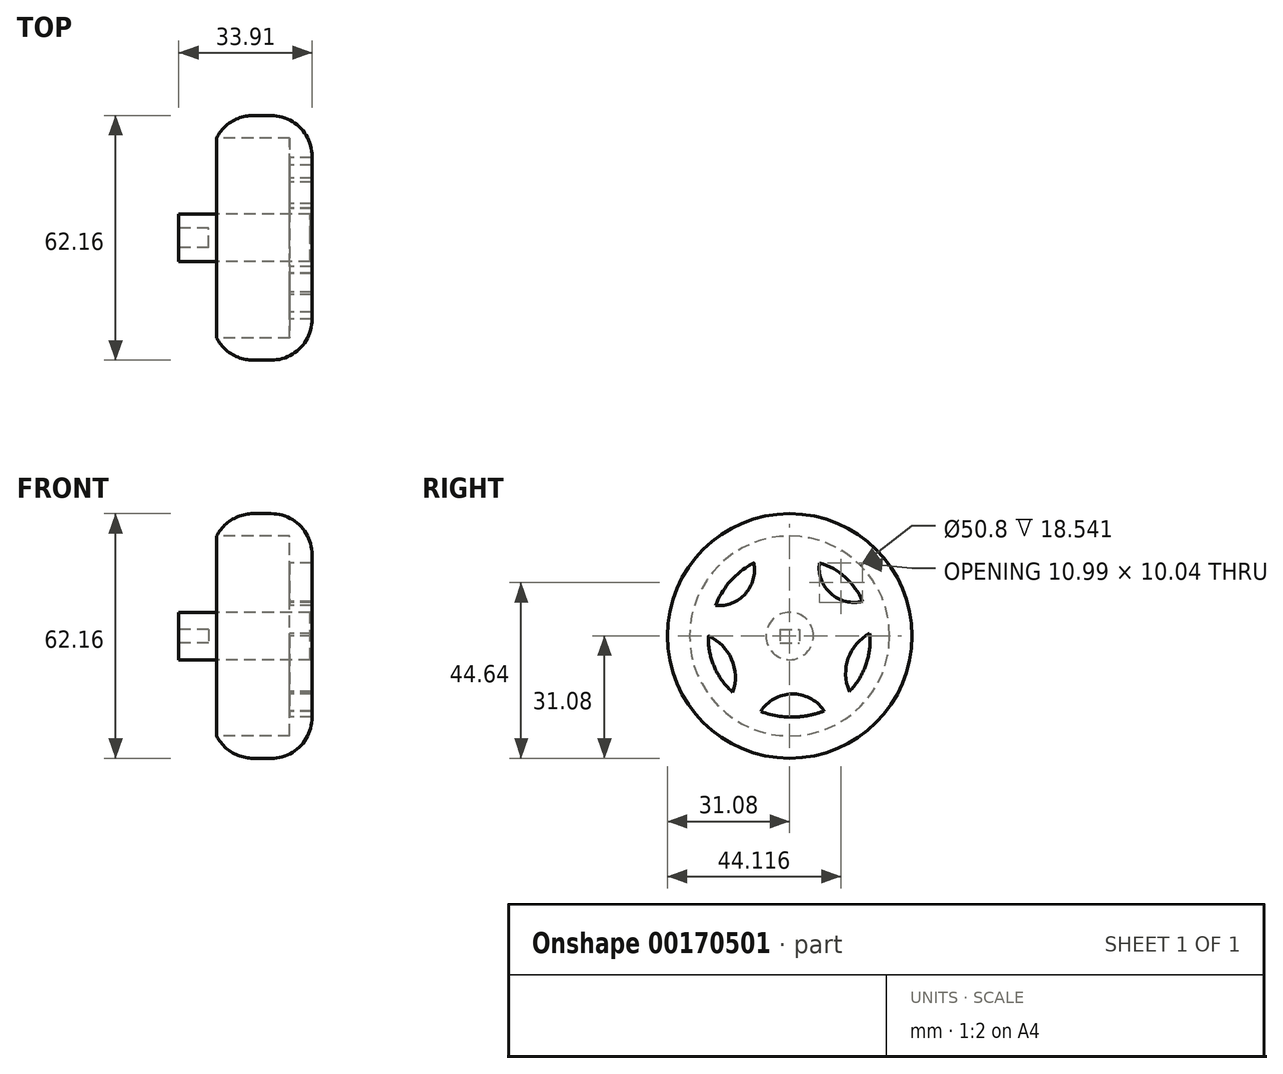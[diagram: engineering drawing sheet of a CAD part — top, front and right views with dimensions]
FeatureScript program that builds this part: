
annotation { "Feature Type Name" : "Feature", "Feature Type Description" : "" }
export const myFeature = defineFeature(function(context is Context, id is Id, definition is map)
    precondition{}
    {
        {
            var Q0;
            Q0=qCreatedBy(makeId("Right.planeOp"),FACE);
            var sketch = newSketch(context, id + "F0", { "sketchPlane" : qUnion([Q0])});
            skCircle(sketch, "E0", {"center": v(0, 0) * mm, "radius": 31.08 * mm});
            skSolve(sketch);
        }
        {
            var Q0;
            Q0 = qSketchRegion(id + "F0", true);
            extrude(context, id + "F1", {"entities" : qUnion([Q0]), "depth" : 25.4 * mm});
        }
        {
            var Q0;
            Q0=makeQuery(id+"F1.opExtrude","CAP_FACE",FACE,{"disambiguationData":[OSD([sQuery(id+"F0.wireOp",EDGE,"E0")])],"isStart":true});
            fillet(context, id + "F2", {"entities" : qUnion([Q0]), "radius" : 10.42 * mm, "tangentPropagation" : true, "allowEdgeOverflow" : false});
        }
        {
            var Q0;
            Q0=makeQuery(id+"F1.opExtrude","CAP_EDGE",EDGE,{"disambiguationData":[OSD([sQuery(id+"F0.wireOp",EDGE,"E0")])],"isStart":false});
            fillet(context, id + "F3", {"entities" : qUnion([Q0]), "radius" : 10.4 * mm, "tangentPropagation" : true, "allowEdgeOverflow" : false});
        }
        {
            var Q0;
            Q0=qCreatedBy(makeId("Right.planeOp"),FACE);
            var sketch = newSketch(context, id + "F4", { "sketchPlane" : qUnion([Q0])});
            skCircle(sketch, "E1", {"center": v(0, 0) * mm, "radius": 25.4 * mm});
            skSolve(sketch);
        }
        {
            var Q0;
            Q0 = qSketchRegion(id + "F4", true);
            extrude(context, id + "F5", {"entities" : qUnion([Q0]), "operationType" : NewBodyOperationType.REMOVE, "depth" : 19.68 * mm});
        }
        {
            var Q0;
            Q0=qCreatedBy(makeId("Right.planeOp"),FACE);
            var sketch = newSketch(context, id + "F6", { "sketchPlane" : qUnion([Q0])});
            skCircle(sketch, "E2", {"center": v(0, 0) * mm, "radius": 6.03 * mm});
            skSolve(sketch);
        }
        {
            var Q0;
            Q0 = qSketchRegion(id + "F6", true);
            extrude(context, id + "F7", {"entities" : qUnion([Q0]), "depth" : 24.9 * mm});
        }
        {
            var Q0;
            Q0=makeQuery(id+"F7.opExtrude","CAP_FACE",FACE,{"disambiguationData":[OSD([sQuery(id+"F6.wireOp",EDGE,"E2")])],"isStart":true});
            extrude(context, id + "F8", {"entities" : qUnion([Q0]), "operationType" : NewBodyOperationType.ADD, "depth" : 8.5 * mm});
        }
        {
            var Q0;
            Q0=makeQuery(id+"F8.opExtrude","CAP_FACE",FACE,{"disambiguationData":[OSD([sQuery(id+"F6.wireOp",EDGE,"E2")])],"isStart":false});
            var sketch = newSketch(context, id + "F9", { "sketchPlane" : qUnion([Q0])});
            skLineSegment(sketch, "E3.bottom", {"start": v(2.46, 1.71) * mm, "end": v(-2.46, 1.71) * mm});
            skLineSegment(sketch, "E3.top", {"start": v(2.46, -1.71) * mm, "end": v(-2.46, -1.71) * mm});
            skLineSegment(sketch, "E3.left", {"start": v(2.46, 1.71) * mm, "end": v(2.46, -1.71) * mm});
            skLineSegment(sketch, "E3.right", {"start": v(-2.46, 1.71) * mm, "end": v(-2.46, -1.71) * mm});
            skPoint(sketch, "E3.middle", {"position": v(0, 0) * mm});
            skSolve(sketch);
        }
        {
            var Q0;
            Q0=makeQuery(id+"F9.imprint","IMPRINT",FACE,{"disambiguationData":[TD([[makeQuery(id+"F9.imprint","IMPRINT",EDGE,{"derivedFrom":sQuery(id+"F9.wireOp",EDGE,"E3.bottom")}),1.0]])]});
            extrude(context, id + "F10", {"entities" : qUnion([Q0]), "operationType" : NewBodyOperationType.REMOVE, "oppositeDirection" : true, "depth" : 7.62 * mm});
        }
        {
            var Q0;
            Q0=qCreatedBy(makeId("Right.planeOp"),FACE);
            var sketch = newSketch(context, id + "F11", { "sketchPlane" : qUnion([Q0])});
            skArc(sketch, "E4", {"start": v(-18.83, 7.76) * mm, "mid": v(-11.26, 10.73) * mm, "end": v(-9.12, 18.58) * mm});
            skArc(sketch, "E5", {"start": v(-9.12, 18.58) * mm, "mid": v(-14.96, 14.05) * mm, "end": v(-18.83, 7.76) * mm});
            skArc(sketch, "E6", {"start": v(-14.47, -14.29) * mm, "mid": v(-14.75, -5.92) * mm, "end": v(-20.68, 0) * mm});
            skArc(sketch, "E7", {"start": v(-20.68, 0) * mm, "mid": v(-19.16, -7.83) * mm, "end": v(-14.47, -14.29) * mm});
            skArc(sketch, "E8", {"start": v(7.57, 18.58) * mm, "mid": v(10.45, 10.78) * mm, "end": v(18.53, 8.81) * mm});
            skArc(sketch, "E9", {"start": v(18.53, 8.81) * mm, "mid": v(14.13, 14.9) * mm, "end": v(7.57, 18.58) * mm});
            skArc(sketch, "E10", {"start": v(8.76, -19.04) * mm, "mid": v(0.67, -14.74) * mm, "end": v(-7.34, -19.17) * mm});
            skArc(sketch, "E11", {"start": v(-7.34, -19.17) * mm, "mid": v(0.72, -20.6) * mm, "end": v(8.76, -19.04) * mm});
            skArc(sketch, "E12", {"start": v(20.33, 0.63) * mm, "mid": v(14.85, -5.7) * mm, "end": v(15.2, -14.08) * mm});
            skArc(sketch, "E13", {"start": v(15.2, -14.08) * mm, "mid": v(19.39, -7.3) * mm, "end": v(20.33, 0.63) * mm});
            skSolve(sketch);
        }
        {
            var Q0;
            Q0 = qSketchRegion(id + "F11", true);
            extrude(context, id + "F12", {"entities" : qUnion([Q0]), "operationType" : NewBodyOperationType.REMOVE, "depth" : 71.12 * mm});
        }
    });
